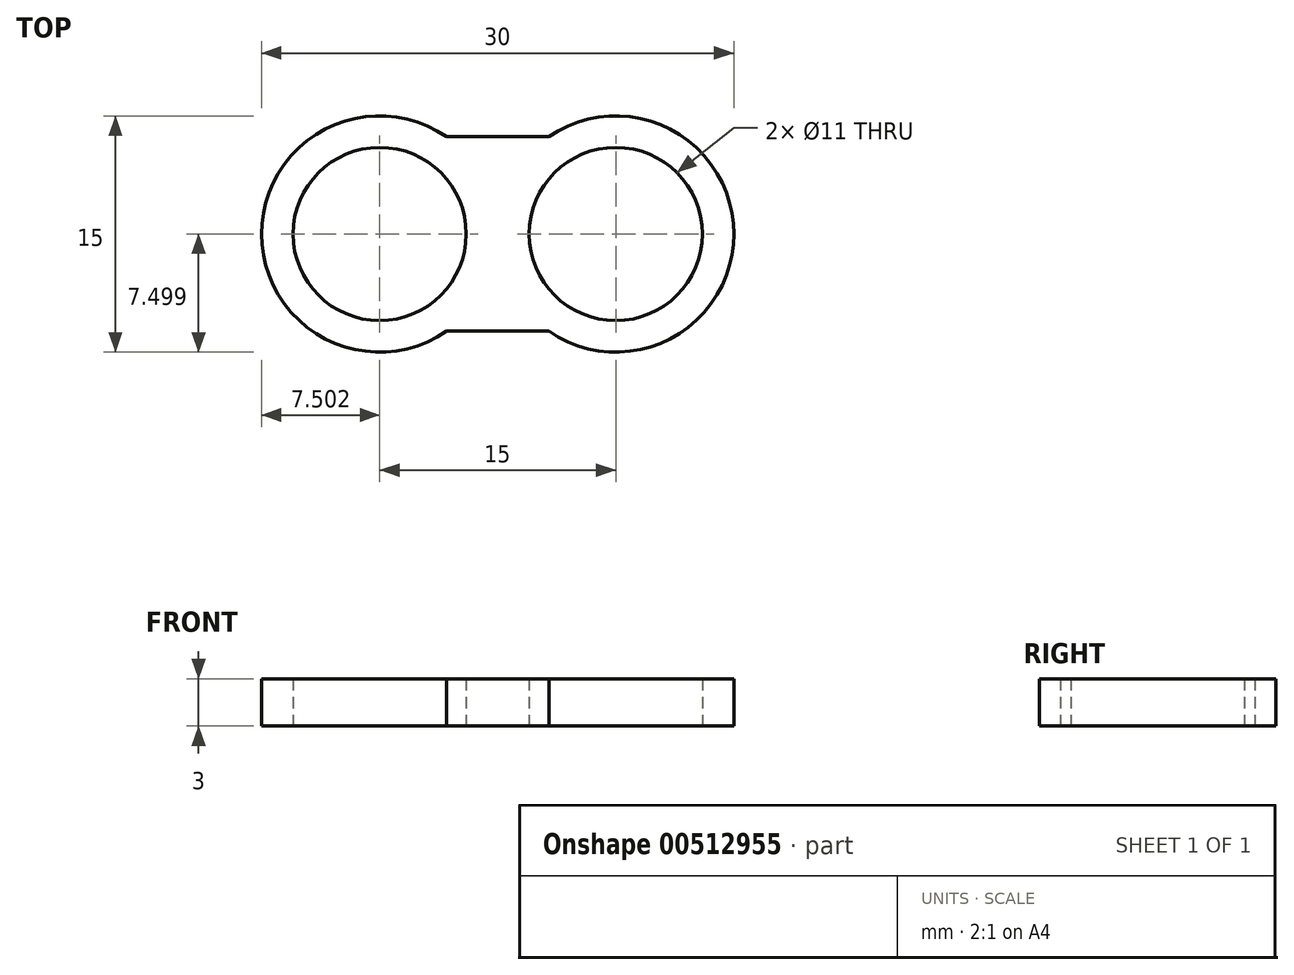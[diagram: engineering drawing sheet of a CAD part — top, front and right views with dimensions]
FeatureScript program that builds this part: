
annotation { "Feature Type Name" : "Feature", "Feature Type Description" : "" }
export const myFeature = defineFeature(function(context is Context, id is Id, definition is map)
    precondition{}
    {
        {
            var Q0;
            Q0=qCreatedBy(makeId("Top.planeOp"),FACE);
            var sketch = newSketch(context, id + "F0", { "sketchPlane" : qUnion([Q0])});
            skLineSegment(sketch, "E0.bottom", {"start": v(-4.24, 6.68) * mm, "end": v(2.25, 6.68) * mm});
            skLineSegment(sketch, "E0.top", {"start": v(-4.24, -5.68) * mm, "end": v(2.25, -5.68) * mm});
            skPoint(sketch, "E0.middle", {"position": v(-1, 0.5) * mm});
            skCircle(sketch, "E1", {"center": v(-8.5, 0.5) * mm, "radius": 7.5 * mm});
            skCircle(sketch, "E2", {"center": v(6.5, 0.5) * mm, "radius": 7.5 * mm});
            skPoint(sketch, "E3.orphan", {"position": v(-8.25, 6.68) * mm});
            skPoint(sketch, "E4.orphan", {"position": v(-8.75, -5.68) * mm});
            skPoint(sketch, "E5.orphan", {"position": v(6.25, -5.68) * mm});
            skPoint(sketch, "E6.orphan", {"position": v(6.75, 6.68) * mm});
            skCircle(sketch, "E7", {"center": v(-8.5, 0.5) * mm, "radius": 5.5 * mm});
            skCircle(sketch, "E8", {"center": v(6.5, 0.5) * mm, "radius": 5.5 * mm});
            skSolve(sketch);
        }
        {
            var Q0;
            Q0=makeQuery(id+"F0.imprint","IMPRINT",FACE,{"disambiguationData":[TD([[makeQuery(id+"F0.imprint","IMPRINT",EDGE,{"derivedFrom":sQuery(id+"F0.wireOp",EDGE,"E7")}),-1.0]])]});
            var Q1;
            {var subQ0=sQuery(id+"F0.wireOp",EDGE,"E0.bottom");Q1=makeQuery(id+"F0.imprint","IMPRINT",FACE,{"disambiguationData":[TD([[makeQuery(id+"F0.imprint","IMPRINT",EDGE,{"derivedFrom":subQ0}),-1.0]])]});}
            var Q2;
            {var subQ0=sQuery(id+"F0.wireOp",EDGE,"E0.top");Q2=makeQuery(id+"F0.imprint","IMPRINT",FACE,{"disambiguationData":[TD([[makeQuery(id+"F0.imprint","IMPRINT",EDGE,{"derivedFrom":subQ0}),1.0]])]});}
            var Q3;
            Q3=makeQuery(id+"F0.imprint","IMPRINT",FACE,{"disambiguationData":[TD([[makeQuery(id+"F0.imprint","IMPRINT",EDGE,{"derivedFrom":sQuery(id+"F0.wireOp",EDGE,"E8")}),-1.0]])]});
            extrude(context, id + "F1", {"entities" : qUnion([Q0, Q1, Q2, Q3]), "depth" : 3 * mm, "offsetDistance" : 25 * mm});
        }
    });
